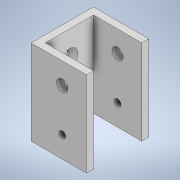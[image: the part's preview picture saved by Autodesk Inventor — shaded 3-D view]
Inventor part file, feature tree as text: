
AUTODESK INVENTOR PART (.ipt)
format: ipt  version: 2020 (Build 240168000, 168)  size: 147,968 bytes
history: native  units: in
note: dims shown in document units (in); Inventor stores cm internally (conversion verified against a paired STEP export)
features: sketch x4, extrude x3, chamfer x2, hole x1
ambient origin geometry x8: Origin, YZ Plane, XZ Plane, XY Plane, X Axis, Y Axis, Z Axis, Center Point
bodies: Solid1 (feature_tree)
feature tree (10):
  extrude  "Extrusion1"  Depth=0.85in
  hole  "Hole1"  [1 undecoded]
  extrude  "Extrusion2"  Depth=1.5in
  extrude  "Extrusion3"  Depth=1.5in
  chamfer  "Chamfer1"  Angle=90.0deg  [1 undecoded]
  chamfer  "Chamfer2"  Distance=0.6in
  sketch  "Sketch1"  dims[d0=0.85in d1=0.85in]
  sketch  "Sketch2"  dims[d2=0.125in d3=0.125in]
  sketch  "Sketch3"  dims[d4=1.5in d5=0.0in d6=0.45in]
  sketch  "Sketch4"  dims[d7=90.0deg d8=0.45in d9=90.0deg d10=0.6in d11=0.17in d12=0.17in d13=0.17in d14=0.3389in d15=0.3in d16=0.09in d17=0.5635in d18=1.0in d19=0.0in d20=0.375in d21=0.2in d22=1.5in d23=0.0in d25=0.375in d26=0.12in d27=1.5in d28=0.0in d29=0.065in d30=0.09in d31=45.0deg d32=0.065in d33=0.09in d34=45.0deg d35=0.5635in d36=0.75in d37=0.8108in d38=0.08in d39=0.75in d40=0.375in]
note: 2 required parameter values undecoded (feature->parameter linkage not recoverable at this tier; creation-order binding heuristic only, values carry confidence <= 0.55)
